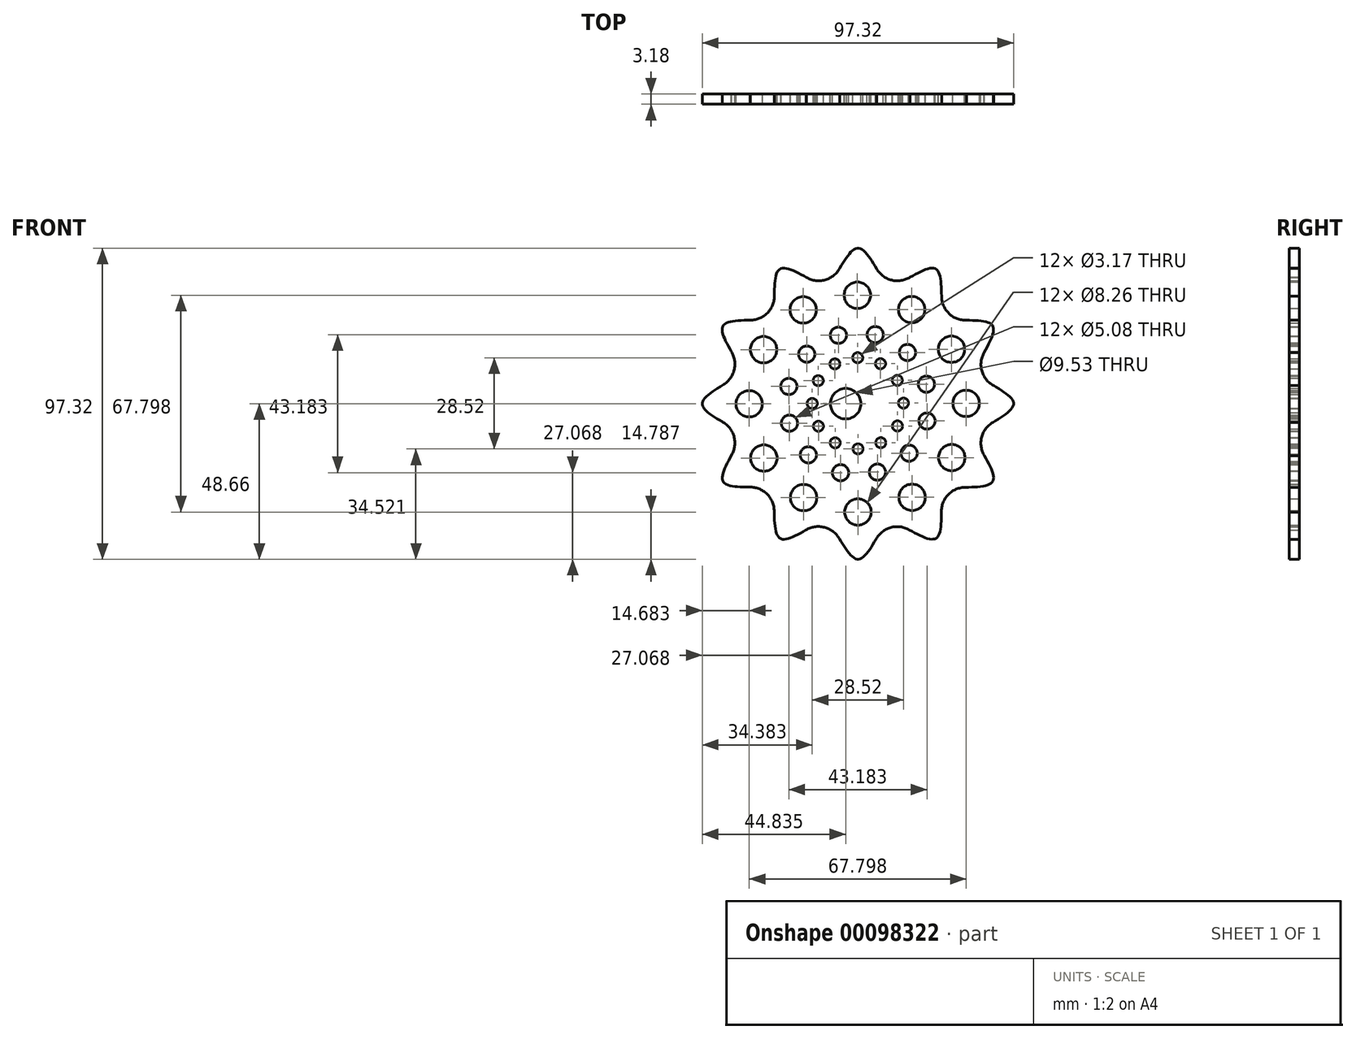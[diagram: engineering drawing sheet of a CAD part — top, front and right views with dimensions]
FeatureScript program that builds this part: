
annotation { "Feature Type Name" : "Feature", "Feature Type Description" : "" }
export const myFeature = defineFeature(function(context is Context, id is Id, definition is map)
    precondition{}
    {
        {
            var Q0;
            Q0=qCreatedBy(makeId("Front.planeOp"),FACE);
            var sketch = newSketch(context, id + "F0", { "sketchPlane" : qUnion([Q0])});
            skPoint(sketch, "E0.center", {"position": v(-1.59, 0.95) * mm});
            skLineSegment(sketch, "E0.anchor1", {"start": v(-1.59, 0.95) * mm, "end": v(0, 37.5) * mm, "construction": true});
            skPoint(sketch, "E1.center", {"position": v(-0.02, 0.12) * mm});
            skPoint(sketch, "E2.center", {"position": v(-0.08, 0.03) * mm});
            skPoint(sketch, "E3.center", {"position": v(0, 0) * mm});
            skArc(sketch, "E4", {"start": v(-16.04, 39.47) * mm, "mid": v(-10.22, 38.74) * mm, "end": v(-5.65, 42.42) * mm});
            skArc(sketch, "E5.1.0", {"start": v(-33.62, 26.16) * mm, "mid": v(-28.22, 28.44) * mm, "end": v(-26.1, 33.91) * mm});
            skArc(sketch, "E5.2.0", {"start": v(-42.2, 5.84) * mm, "mid": v(-38.66, 10.52) * mm, "end": v(-39.57, 16.32) * mm});
            skArc(sketch, "E5.3.0", {"start": v(-39.47, -16.04) * mm, "mid": v(-38.74, -10.22) * mm, "end": v(-42.42, -5.65) * mm});
            skArc(sketch, "E5.4.0", {"start": v(-26.16, -33.62) * mm, "mid": v(-28.44, -28.22) * mm, "end": v(-33.91, -26.1) * mm});
            skArc(sketch, "E5.5.0", {"start": v(-5.84, -42.2) * mm, "mid": v(-10.52, -38.66) * mm, "end": v(-16.32, -39.57) * mm});
            skArc(sketch, "E5.6.0", {"start": v(16.04, -39.47) * mm, "mid": v(10.22, -38.74) * mm, "end": v(5.65, -42.42) * mm});
            skArc(sketch, "E5.7.0", {"start": v(33.62, -26.16) * mm, "mid": v(28.22, -28.44) * mm, "end": v(26.1, -33.91) * mm});
            skArc(sketch, "E5.8.0", {"start": v(42.2, -5.84) * mm, "mid": v(38.66, -10.52) * mm, "end": v(39.57, -16.32) * mm});
            skArc(sketch, "E5.9.0", {"start": v(39.47, 16.04) * mm, "mid": v(38.74, 10.22) * mm, "end": v(42.42, 5.65) * mm});
            skArc(sketch, "E5.10.0", {"start": v(26.16, 33.62) * mm, "mid": v(28.44, 28.22) * mm, "end": v(33.91, 26.1) * mm});
            skArc(sketch, "E5.11.0", {"start": v(5.84, 42.2) * mm, "mid": v(10.52, 38.66) * mm, "end": v(16.32, 39.57) * mm});
            skCircle(sketch, "E6", {"center": v(-0.07, 14.38) * mm, "radius": 1.59 * mm});
            skCircle(sketch, "E7.1.0", {"center": v(-7.2, 12.44) * mm, "radius": 1.59 * mm});
            skCircle(sketch, "E7.2.0", {"center": v(-12.4, 7.2) * mm, "radius": 1.59 * mm});
            skCircle(sketch, "E7.3.0", {"center": v(-14.28, 0.07) * mm, "radius": 1.59 * mm});
            skCircle(sketch, "E7.4.0", {"center": v(-12.34, -7.05) * mm, "radius": 1.59 * mm});
            skCircle(sketch, "E7.5.0", {"center": v(-7.1, -12.25) * mm, "radius": 1.59 * mm});
            skCircle(sketch, "E7.6.0", {"center": v(0.03, -14.14) * mm, "radius": 1.59 * mm});
            skCircle(sketch, "E7.7.0", {"center": v(7.16, -12.2) * mm, "radius": 1.59 * mm});
            skCircle(sketch, "E7.8.0", {"center": v(12.36, -6.96) * mm, "radius": 1.59 * mm});
            skCircle(sketch, "E7.9.0", {"center": v(14.24, 0.17) * mm, "radius": 1.59 * mm});
            skCircle(sketch, "E7.10.0", {"center": v(12.3, 7.3) * mm, "radius": 1.59 * mm});
            skCircle(sketch, "E7.11.0", {"center": v(7.07, 12.5) * mm, "radius": 1.59 * mm});
            skFitSpline(sketch, "E8", {"points": [v(-5.65, 42.42) * mm, v(0, 48.66) * mm, v(5.84, 42.2) * mm], "startDerivative": vector(11.36, 18.86) * mm, "endDerivative": vector(11.63, -19.2) * mm});
            skFitSpline(sketch, "E9", {"points": [v(-16.04, 39.47) * mm, v(-24.35, 42.12) * mm, v(-26.1, 33.91) * mm], "startDerivative": vector(-19.73, 10.78) * mm, "endDerivative": vector(-0.34, -21.99) * mm});
            skFitSpline(sketch, "E10", {"points": [v(-33.62, 26.16) * mm, v(-42.15, 24.3) * mm, v(-39.57, 16.32) * mm], "startDerivative": vector(-22.48, -0.53) * mm, "endDerivative": vector(10.7, -19.21) * mm});
            skFitSpline(sketch, "E11", {"points": [v(-42.2, 5.84) * mm, v(-48.66, -0.03) * mm, v(-42.42, -5.65) * mm], "startDerivative": vector(-19.2, -11.7) * mm, "endDerivative": vector(18.87, -11.29) * mm});
            skFitSpline(sketch, "E12", {"points": [v(16.32, 39.57) * mm, v(24.3, 42.15) * mm, v(26.16, 33.62) * mm], "startDerivative": vector(19.21, 10.7) * mm, "endDerivative": vector(0.53, -22.48) * mm});
            skFitSpline(sketch, "E13", {"points": [v(33.91, 26.1) * mm, v(42.12, 24.35) * mm, v(39.47, 16.04) * mm], "startDerivative": vector(21.99, -0.34) * mm, "endDerivative": vector(-10.78, -19.73) * mm});
            skFitSpline(sketch, "E14", {"points": [v(-39.47, -16.04) * mm, v(-42.12, -24.35) * mm, v(-33.91, -26.1) * mm], "startDerivative": vector(-10.78, -19.73) * mm, "endDerivative": vector(21.99, -0.34) * mm});
            skFitSpline(sketch, "E15", {"points": [v(-26.16, -33.62) * mm, v(-24.3, -42.15) * mm, v(-16.32, -39.57) * mm], "startDerivative": vector(0.53, -22.48) * mm, "endDerivative": vector(19.21, 10.7) * mm});
            skFitSpline(sketch, "E16", {"points": [v(-5.84, -42.2) * mm, v(0.03, -48.66) * mm, v(5.65, -42.42) * mm], "startDerivative": vector(11.7, -19.2) * mm, "endDerivative": vector(11.29, 18.87) * mm});
            skFitSpline(sketch, "E17", {"points": [v(16.04, -39.47) * mm, v(24.35, -42.12) * mm, v(26.1, -33.91) * mm], "startDerivative": vector(19.73, -10.78) * mm, "endDerivative": vector(0.34, 21.99) * mm});
            skFitSpline(sketch, "E18", {"points": [v(33.62, -26.16) * mm, v(42.15, -24.3) * mm, v(39.57, -16.32) * mm], "startDerivative": vector(22.48, 0.53) * mm, "endDerivative": vector(-10.7, 19.21) * mm});
            skFitSpline(sketch, "E19", {"points": [v(42.42, 5.65) * mm, v(48.66, 0.03) * mm, v(42.2, -5.84) * mm], "startDerivative": vector(18.87, -11.29) * mm, "endDerivative": vector(-19.2, -11.7) * mm});
            skCircle(sketch, "E20", {"center": v(-3.83, 0) * mm, "radius": 4.76 * mm});
            skCircle(sketch, "E21", {"center": v(-0.15, 33.93) * mm, "radius": 4.13 * mm});
            skCircle(sketch, "E22.1.0", {"center": v(-17.1, 29.35) * mm, "radius": 4.13 * mm});
            skCircle(sketch, "E22.2.0", {"center": v(-29.47, 16.9) * mm, "radius": 4.13 * mm});
            skCircle(sketch, "E22.3.0", {"center": v(-33.98, -0.05) * mm, "radius": 4.13 * mm});
            skCircle(sketch, "E22.4.0", {"center": v(-29.4, -17) * mm, "radius": 4.13 * mm});
            skCircle(sketch, "E22.5.0", {"center": v(-16.96, -29.37) * mm, "radius": 4.13 * mm});
            skCircle(sketch, "E22.6.0", {"center": v(0, -33.87) * mm, "radius": 4.13 * mm});
            skCircle(sketch, "E22.7.0", {"center": v(16.94, -29.3) * mm, "radius": 4.13 * mm});
            skCircle(sketch, "E22.8.0", {"center": v(29.32, -16.86) * mm, "radius": 4.13 * mm});
            skCircle(sketch, "E22.9.0", {"center": v(33.82, 0.1) * mm, "radius": 4.13 * mm});
            skCircle(sketch, "E22.10.0", {"center": v(29.24, 17.04) * mm, "radius": 4.13 * mm});
            skCircle(sketch, "E22.11.0", {"center": v(16.8, 29.42) * mm, "radius": 4.13 * mm});
            skCircle(sketch, "E23", {"center": v(-21.6, 5.42) * mm, "radius": 2.54 * mm});
            skCircle(sketch, "E24.1.0", {"center": v(-21.4, -6.1) * mm, "radius": 2.54 * mm});
            skCircle(sketch, "E24.2.0", {"center": v(-15.49, -16) * mm, "radius": 2.54 * mm});
            skCircle(sketch, "E24.3.0", {"center": v(-5.42, -21.6) * mm, "radius": 2.54 * mm});
            skCircle(sketch, "E24.4.0", {"center": v(6.1, -21.4) * mm, "radius": 2.54 * mm});
            skCircle(sketch, "E24.5.0", {"center": v(16, -15.49) * mm, "radius": 2.54 * mm});
            skCircle(sketch, "E24.6.0", {"center": v(21.6, -5.42) * mm, "radius": 2.54 * mm});
            skCircle(sketch, "E24.7.0", {"center": v(21.4, 6.1) * mm, "radius": 2.54 * mm});
            skCircle(sketch, "E24.8.0", {"center": v(15.49, 16) * mm, "radius": 2.54 * mm});
            skCircle(sketch, "E24.9.0", {"center": v(5.42, 21.6) * mm, "radius": 2.54 * mm});
            skCircle(sketch, "E24.10.0", {"center": v(-6.1, 21.4) * mm, "radius": 2.54 * mm});
            skCircle(sketch, "E24.11.0", {"center": v(-16, 15.49) * mm, "radius": 2.54 * mm});
            skSolve(sketch);
        }
        {
            var Q0;
            Q0 = qSketchRegion(id + "F0", true);
            extrude(context, id + "F1", {"entities" : qUnion([Q0]), "depth" : 3.17 * mm});
        }
    });
